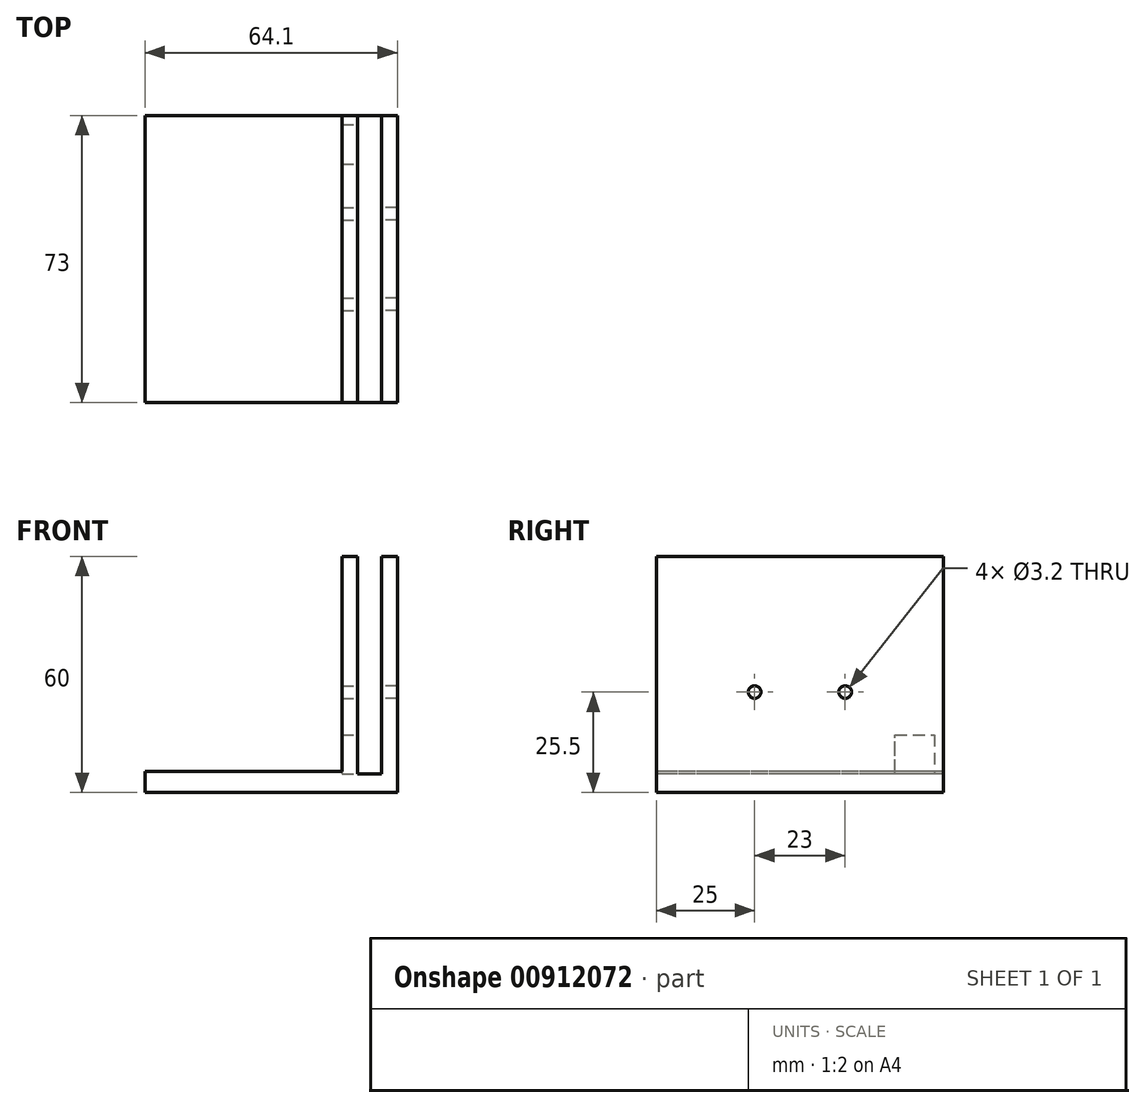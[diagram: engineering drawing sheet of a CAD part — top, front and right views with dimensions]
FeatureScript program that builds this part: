
annotation { "Feature Type Name" : "Feature", "Feature Type Description" : "" }
export const myFeature = defineFeature(function(context is Context, id is Id, definition is map)
    precondition{}
    {
        {
            var Q0;
            Q0=qCreatedBy(makeId("Right.planeOp"),FACE);
            var sketch = newSketch(context, id + "F0", { "sketchPlane" : qUnion([Q0])});
            skLineSegment(sketch, "E0.bottom", {"start": v(0, 0) * mm, "end": v(32, 0) * mm});
            skLineSegment(sketch, "E0.top", {"start": v(0, 60) * mm, "end": v(32, 60) * mm});
            skCircle(sketch, "E1", {"center": v(4.5, 25.5) * mm, "radius": 1.6 * mm});
            skCircle(sketch, "E2", {"center": v(27.5, 25.5) * mm, "radius": 1.6 * mm});
            skLineSegment(sketch, "E3", {"start": v(0, 60) * mm, "end": v(-20.5, 60) * mm});
            skLineSegment(sketch, "E4", {"start": v(-20.5, 60) * mm, "end": v(-20.5, 0) * mm});
            skLineSegment(sketch, "E5", {"start": v(-20.5, 0) * mm, "end": v(0, 0) * mm});
            skLineSegment(sketch, "E6", {"start": v(32, 60) * mm, "end": v(52.5, 60) * mm});
            skLineSegment(sketch, "E7", {"start": v(52.5, 60) * mm, "end": v(52.5, 0) * mm});
            skLineSegment(sketch, "E8", {"start": v(52.5, 0) * mm, "end": v(32, 0) * mm});
            skSolve(sketch);
        }
        {
            var Q0;
            Q0 = qSketchRegion(id + "F0", true);
            extrude(context, id + "F1", {"entities" : qUnion([Q0]), "depth" : 4 * mm, "offsetDistance" : 25 * mm});
        }
        {
            var Q0;
            Q0=makeQuery(id+"F1.opExtrude","CAP_FACE",FACE,{"disambiguationData":[OSD([sQuery(id+"F0.wireOp",EDGE,"E0.bottom"),sQuery(id+"F0.wireOp",EDGE,"E0.top"),sQuery(id+"F0.wireOp",EDGE,"E1"),sQuery(id+"F0.wireOp",EDGE,"E2"),sQuery(id+"F0.wireOp",EDGE,"E3"),sQuery(id+"F0.wireOp",EDGE,"E4"),sQuery(id+"F0.wireOp",EDGE,"E5"),sQuery(id+"F0.wireOp",EDGE,"E6"),sQuery(id+"F0.wireOp",EDGE,"E7"),sQuery(id+"F0.wireOp",EDGE,"E8")])],"isStart":true});
            var sketch = newSketch(context, id + "F2", { "sketchPlane" : qUnion([Q0])});
            skLineSegment(sketch, "E9.bottom", {"start": v(-52.5, 0) * mm, "end": v(20.5, 0) * mm});
            skLineSegment(sketch, "E9.top", {"start": v(-52.5, 4.65) * mm, "end": v(20.5, 4.65) * mm});
            skLineSegment(sketch, "E9.left", {"start": v(-52.5, 0) * mm, "end": v(-52.5, 4.65) * mm});
            skLineSegment(sketch, "E9.right", {"start": v(20.5, 0) * mm, "end": v(20.5, 4.65) * mm});
            skSolve(sketch);
        }
        {
            var Q0;
            Q0 = qSketchRegion(id + "F2", true);
            extrude(context, id + "F3", {"entities" : qUnion([Q0]), "operationType" : NewBodyOperationType.ADD, "depth" : 6.1 * mm, "offsetDistance" : 25 * mm});
        }
        {
            var Q0;
            Q0=makeQuery(id+"F3.opExtrude","CAP_FACE",FACE,{"disambiguationData":[OSD([sQuery(id+"F2.wireOp",EDGE,"E9.bottom"),sQuery(id+"F2.wireOp",EDGE,"E9.top"),sQuery(id+"F2.wireOp",EDGE,"E9.left"),sQuery(id+"F2.wireOp",EDGE,"E9.right")])],"isStart":false});
            var sketch = newSketch(context, id + "F4", { "sketchPlane" : qUnion([Q0])});
            skLineSegment(sketch, "E10.bottom", {"start": v(-52.5, 0) * mm, "end": v(20.5, 0) * mm});
            skLineSegment(sketch, "E10.top", {"start": v(-52.5, 60) * mm, "end": v(20.5, 60) * mm});
            skLineSegment(sketch, "E10.left", {"start": v(-52.5, 0) * mm, "end": v(-52.5, 60) * mm});
            skLineSegment(sketch, "E10.right", {"start": v(20.5, 0) * mm, "end": v(20.5, 60) * mm});
            skCircle(sketch, "E11", {"center": v(-27.5, 25.5) * mm, "radius": 1.6 * mm});
            skCircle(sketch, "E12", {"center": v(-4.5, 25.5) * mm, "radius": 1.6 * mm});
            skLineSegment(sketch, "E13", {"start": v(-40.12, 4.65) * mm, "end": v(-40.12, 14.65) * mm});
            skLineSegment(sketch, "E14", {"start": v(-40.12, 14.65) * mm, "end": v(-50.12, 14.65) * mm});
            skLineSegment(sketch, "E15", {"start": v(-50.12, 14.65) * mm, "end": v(-50.12, 4.65) * mm});
            skLineSegment(sketch, "E16", {"start": v(-50.12, 4.65) * mm, "end": v(-40.12, 4.65) * mm});
            skSolve(sketch);
        }
        {
            var Q0;
            Q0 = qSketchRegion(id + "F4", true);
            extrude(context, id + "F5", {"entities" : qUnion([Q0]), "operationType" : NewBodyOperationType.ADD, "depth" : 4 * mm, "offsetDistance" : 25 * mm});
        }
        {
            var Q0;
            Q0=makeQuery(id+"F5.opExtrude","CAP_FACE",FACE,{"disambiguationData":[OSD([sQuery(id+"F4.wireOp",EDGE,"E10.bottom"),sQuery(id+"F4.wireOp",EDGE,"E10.top"),sQuery(id+"F4.wireOp",EDGE,"E10.left"),sQuery(id+"F4.wireOp",EDGE,"E10.right")])],"isStart":false});
            var sketch = newSketch(context, id + "F6", { "sketchPlane" : qUnion([Q0])});
            skLineSegment(sketch, "E17.bottom", {"start": v(-52.5, 0) * mm, "end": v(20.5, 0) * mm});
            skLineSegment(sketch, "E17.top", {"start": v(-52.5, 5.37) * mm, "end": v(20.5, 5.37) * mm});
            skLineSegment(sketch, "E17.left", {"start": v(-52.5, 0) * mm, "end": v(-52.5, 5.37) * mm});
            skLineSegment(sketch, "E17.right", {"start": v(20.5, 0) * mm, "end": v(20.5, 5.37) * mm});
            skSolve(sketch);
        }
        {
            var Q0;
            Q0 = qSketchRegion(id + "F6", true);
            extrude(context, id + "F7", {"entities" : qUnion([Q0]), "operationType" : NewBodyOperationType.ADD, "depth" : 50 * mm, "offsetDistance" : 25 * mm});
        }
    });
